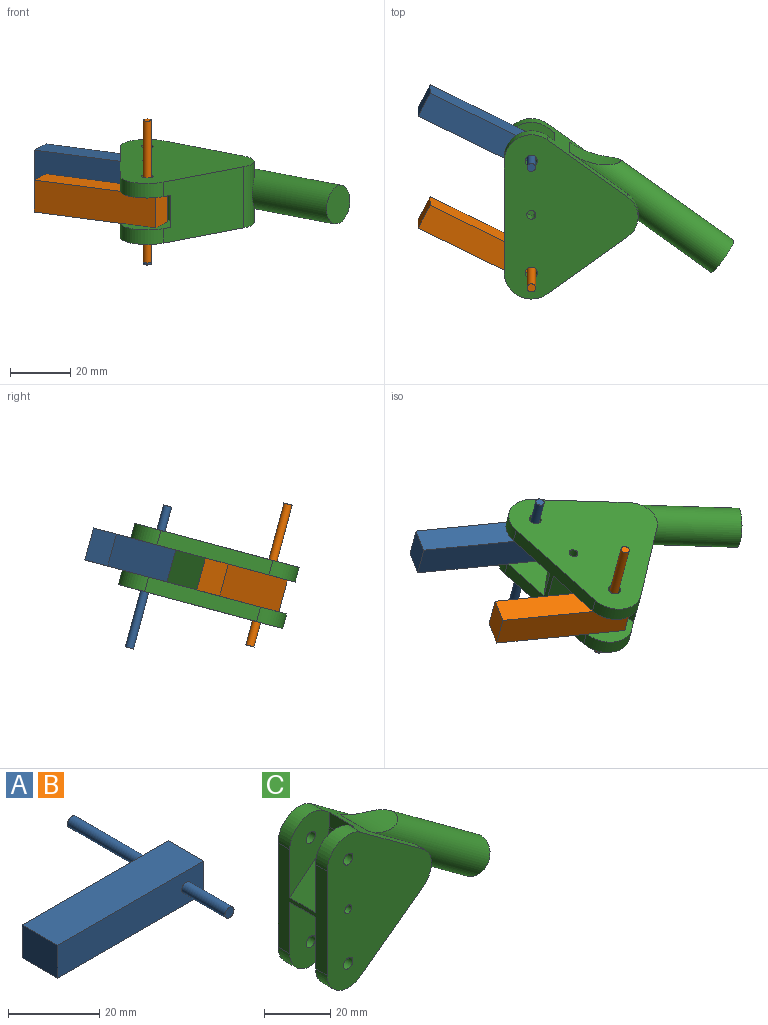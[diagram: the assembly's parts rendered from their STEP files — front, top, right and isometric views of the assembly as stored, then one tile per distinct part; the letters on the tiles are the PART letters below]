
ASSEMBLY  parts=3 mates=3
PART A: 10 faces, bbox 45.3x48.8x8.8 mm
  f0: plane 45.28x8.8mm, normal (0,-1,0), area 392.3mm2, adj f1,f2,f4,f5,f8
  f1: plane 11x8.8mm, normal (1,0,0), area 96.8mm2, adj f0,f2,f3,f4
  f2: plane 45.28x11mm, normal (0,0,-1), area 498.1mm2, adj f0,f1,f3,f5
  f3: plane 45.28x8.8mm, normal (0,1,0), area 392.3mm2, adj f1,f2,f4,f5,f7
  f4: plane 45.28x11mm, normal (0,0,1), area 498.1mm2, adj f0,f1,f3,f5
  f5: plane 11x8.8mm, normal (-1,0,0), area 96.8mm2, adj f0,f2,f3,f4
  f6: plane 2.8x2.8mm, normal (0,1,0), area 6.2mm2, adj f7
  f7: cylinder r=1.4mm len=24.4mm, axis (0,1,0), area 214.6mm2, adj f3,f6
  f8: cylinder r=1.4mm len=13.4mm, axis (0,1,0), area 117.9mm2, adj f0,f9
  f9: plane 2.8x2.8mm, normal (0,-1,0), area 6.2mm2, adj f8
PART B: same geometry as A
PART C: 31 faces, bbox 76.3x21x56.5 mm
  f0: cylinder r=2mm len=5mm, axis (0,1,0), area 62.8mm2, adj f13,f23
  f1: cylinder r=9mm len=14.34mm, axis (0,1,0), area 99.3mm2, adj f4,f8,f13,f23
  f2: cylinder r=9mm len=14.34mm, axis (0,1,0), area 99.3mm2, adj f4,f6,f13,f18
  f3: cylinder r=2mm len=5mm, axis (0,1,0), area 62.8mm2, adj f13,f18
  f4: plane 38.5x21mm, normal (-1,0,0), area 403.1mm2, adj f1,f2,f5,f10,f12,f13,f16,f17
  f5: cylinder r=9mm len=14.34mm, axis (0,1,0), area 99.3mm2, adj f4,f6,f12,f17
  f6: plane 26.69x21mm, normal (0.59,0,-0.81), area 662.4mm2, adj f2,f5,f7,f12,f13,f14,f17,f18
  f7: cylinder r=8.49mm len=21mm, axis (0,1,0), area 207mm2, adj f6,f8,f12,f13,f24
  f8: plane 26.69x21mm, normal (0.59,0,0.81), area 348.6mm2, adj f1,f7,f10,f12,f13,f20,f22,f23
  f9: cylinder r=2mm len=5mm, axis (0,1,0), area 62.8mm2, adj f12,f22
  f10: cylinder r=9mm len=14.34mm, axis (0,1,0), area 99.3mm2, adj f4,f8,f12,f22
  f11: cylinder r=2mm len=5mm, axis (0,1,0), area 62.8mm2, adj f12,f17
  f12: plane 56.5x44.49mm, normal (0,-1,0), area 1660mm2, adj f4,f5,f6,f7,f8,f9,f10,f11
  f13: plane 56.5x44.49mm, normal (0,1,0), area 1660mm2, adj f0,f1,f2,f3,f4,f6,f7,f8
  f14: plane 11x5.43mm, normal (-1,0,0), area 59.7mm2, adj f6,f15,f17,f18
  f15: cylinder r=7.81mm len=11mm, axis (0,1,0), area 70.5mm2, adj f14,f16,f17,f18
  f16: plane 14.33x13.37mm, normal (-0.68,0,-0.73), area 215.6mm2, adj f4,f15,f17,f18
  f17: plane 28.08x16.81mm, normal (0,1,0), area 299.2mm2, adj f4,f5,f6,f11,f14,f15,f16
  f18: plane 28.08x16.81mm, normal (0,-1,0), area 299.2mm2, adj f2,f3,f4,f6,f14,f15,f16
  f19: cylinder r=7.81mm len=11mm, axis (0,1,0), area 74.9mm2, adj f20,f21,f22,f23
  f20: plane 11x5.43mm, normal (-1,0,0), area 59.7mm2, adj f8,f19,f22,f23
  f21: plane 14.03x11.8mm, normal (-0.64,0,0.77), area 201.7mm2, adj f4,f19,f22,f23
  f22: plane 26.78x16.81mm, normal (0,1,0), area 289.9mm2, adj f4,f8,f9,f10,f19,f20,f21
  f23: plane 26.78x16.81mm, normal (0,-1,0), area 289.9mm2, adj f0,f1,f4,f8,f19,f20,f21
  f24: cylinder r=6.5mm len=58.55mm, axis (-0.81,0,0.59), area 1685.2mm2, adj f7,f8,f25,f26
  f25: plane 13x10.47mm, normal (0.81,0,-0.59), area 132.7mm2, adj f24
  f26: cylinder r=24.14mm len=17.12mm, axis (0,-1,0), area 205.2mm2, adj f8,f24
  f27: cylinder r=1.5mm len=6mm, axis (0,1,0), area 56.5mm2, adj f13,f28
  f28: plane 3x3mm, normal (0,1,0), area 7.1mm2, adj f27
  f29: cylinder r=1.5mm len=5mm, axis (0,-1,0), area 47.1mm2, adj f12,f30
  f30: plane 3x3mm, normal (0,-1,0), area 7.1mm2, adj f29
PLACE A rot(axis=(-0.93,0.29,-0.22),79deg) t=(-41.95,-31.47,40.97)mm
PLACE B rot(axis=(0.96,-0.17,-0.23),107.4deg) t=(-7.3,-7.67,69.09)mm
PLACE C rot(axis=(-1,0,0),75deg) t=(-24.62,-35.45,39.9)mm fixed
MATE revolute B.f7 <-> C.f15  axis (0,0.26,-0.97) through (-24.62,-36.74,44.73)mm
MATE revolute A.f7 <-> C.f1  axis (0,0.26,-0.97) through (-24.62,-2.4,65.32)mm
MATE parallel A.f2 <-> B.f2  axis (-0.45,-0.86,-0.23) through (-42,2.72,61)mm
